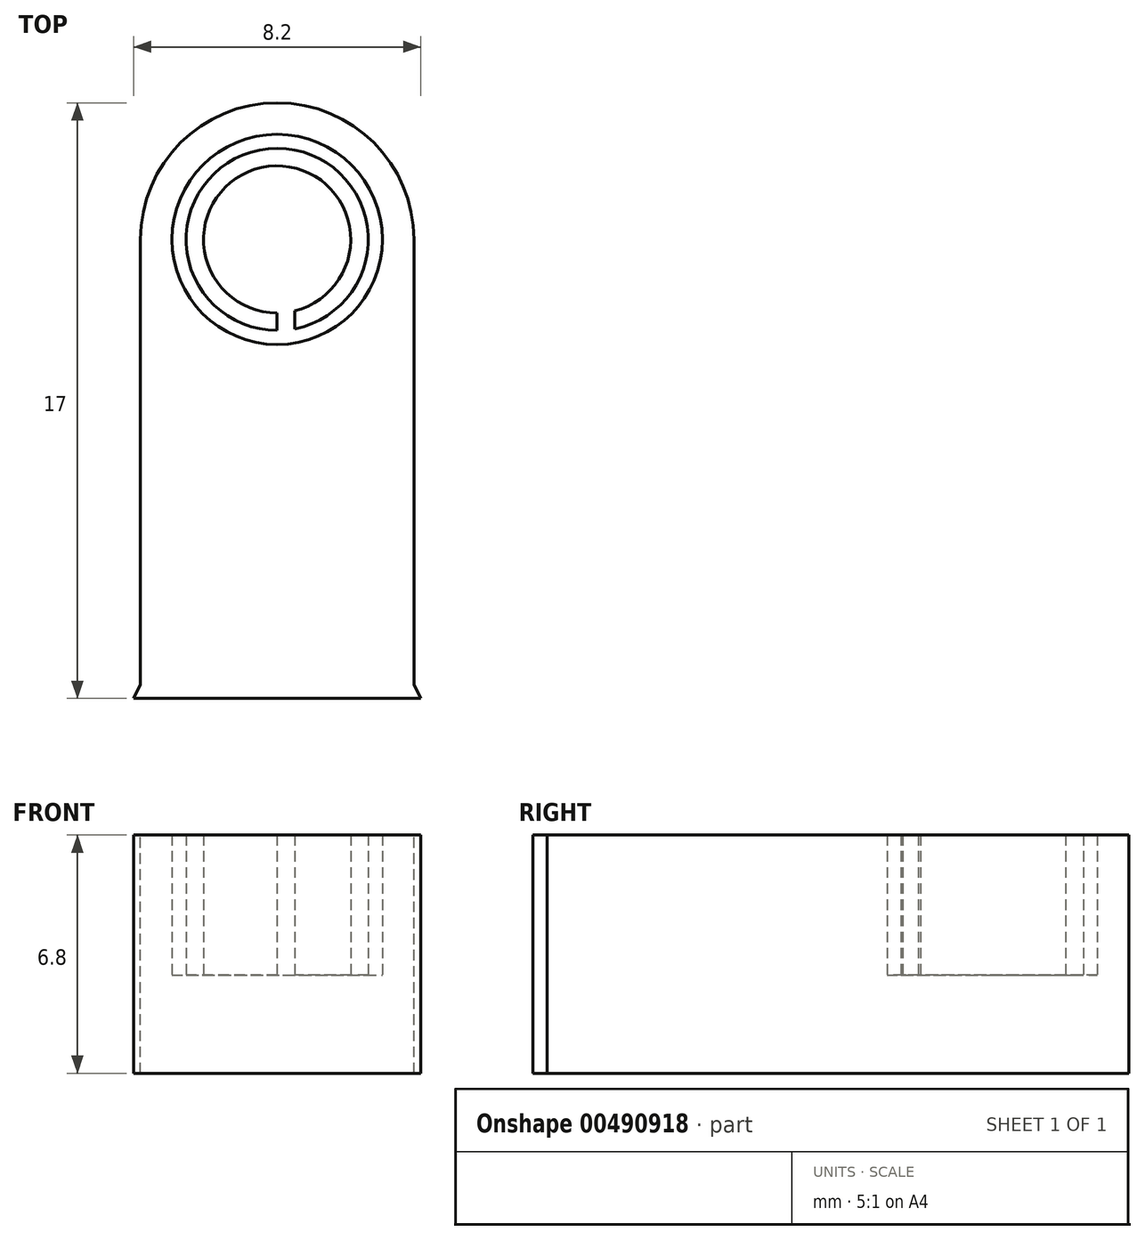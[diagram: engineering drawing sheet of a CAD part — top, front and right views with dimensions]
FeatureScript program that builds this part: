
annotation { "Feature Type Name" : "Feature", "Feature Type Description" : "" }
export const myFeature = defineFeature(function(context is Context, id is Id, definition is map)
    precondition{}
    {
        {
            var Q0;
            Q0=qCreatedBy(makeId("Top.planeOp"),FACE);
            var sketch = newSketch(context, id + "F0", { "sketchPlane" : qUnion([Q0])});
            skLineSegment(sketch, "E0", {"start": v(0, 0) * mm, "end": v(0, 12.7) * mm});
            skLineSegment(sketch, "E1", {"start": v(3.9, 16.6) * mm, "end": v(3.9, 16.6) * mm});
            skLineSegment(sketch, "E2", {"start": v(7.8, 12.7) * mm, "end": v(7.8, 0) * mm});
            skLineSegment(sketch, "E3", {"start": v(7.8, 0) * mm, "end": v(8, -0.4) * mm});
            skLineSegment(sketch, "E4", {"start": v(8, -0.4) * mm, "end": v(-0.2, -0.4) * mm});
            skLineSegment(sketch, "E5", {"start": v(-0.2, -0.4) * mm, "end": v(0, 0) * mm});
            skPoint(sketch, "E6.visualSharp", {"position": v(0, 16.6) * mm});
            skArc(sketch, "E6.filletArc", {"start": v(3.9, 16.6) * mm, "mid": v(1.14, 15.46) * mm, "end": v(0, 12.7) * mm});
            skPoint(sketch, "E7.visualSharp", {"position": v(7.8, 16.6) * mm});
            skArc(sketch, "E7.filletArc", {"start": v(7.8, 12.7) * mm, "mid": v(6.66, 15.46) * mm, "end": v(3.9, 16.6) * mm});
            skCircle(sketch, "E8", {"center": v(3.9, 12.7) * mm, "radius": 2.1 * mm});
            skCircle(sketch, "E9", {"center": v(3.9, 12.7) * mm, "radius": 2.6 * mm});
            skCircle(sketch, "E10", {"center": v(3.9, 12.7) * mm, "radius": 3 * mm});
            skLineSegment(sketch, "E11", {"start": v(3.9, 10.6) * mm, "end": v(3.9, 10.1) * mm});
            skLineSegment(sketch, "E12", {"start": v(3.4, 10.66) * mm, "end": v(3.4, 10.15) * mm});
            skSolve(sketch);
        }
        {
            var Q0;
            Q0=makeQuery(id+"F0.imprint","IMPRINT",FACE,{"disambiguationData":[TD([[makeQuery(id+"F0.imprint","IMPRINT",EDGE,{"derivedFrom":sQuery(id+"F0.wireOp",EDGE,"E0")}),-1.0]])]});
            var Q1;
            {var subQ0=sQuery(id+"F0.wireOp",EDGE,"E8");var subQ1=makeQuery(id+"F0.imprint","INTERSECT",VERTEX,{"derivedFrom":[subQ0,sQuery(id+"F0.wireOp",EDGE,"E11")]});Q1=makeQuery(id+"F0.imprint","IMPRINT",FACE,{"disambiguationData":[TD([[makeQuery(id+"F0.imprint","IMPRINT",EDGE,{"disambiguationData":[TD([[subQ1,1.0]])],"derivedFrom":subQ0}),1.0]])]});}
            var Q2;
            Q2=makeQuery(id+"F0.imprint","IMPRINT",FACE,{"disambiguationData":[TD([[makeQuery(id+"F0.imprint","IMPRINT",EDGE,{"derivedFrom":sQuery(id+"F0.wireOp",EDGE,"E10")}),1.0]])]});
            var Q3;
            {var subQ0=sQuery(id+"F0.wireOp",EDGE,"E11");Q3=makeQuery(id+"F0.imprint","IMPRINT",FACE,{"disambiguationData":[TD([[makeQuery(id+"F0.imprint","IMPRINT",EDGE,{"derivedFrom":subQ0}),1.0]])]});}
            var Q4;
            {var subQ0=sQuery(id+"F0.wireOp",EDGE,"E11");Q4=makeQuery(id+"F0.imprint","IMPRINT",FACE,{"disambiguationData":[TD([[makeQuery(id+"F0.imprint","IMPRINT",EDGE,{"derivedFrom":subQ0}),-1.0]])]});}
            extrude(context, id + "F1", {"entities" : qUnion([Q0, Q1, Q2, Q3, Q4]), "depth" : 2.8 * mm});
        }
        {
            var Q0;
            Q0 = qSketchRegion(id + "F0", true);
            var Q1;
            {var subQ0=sQuery(id+"F0.wireOp",EDGE,"E11");Q1=makeQuery(id+"F0.imprint","IMPRINT",FACE,{"disambiguationData":[TD([[makeQuery(id+"F0.imprint","IMPRINT",EDGE,{"derivedFrom":subQ0}),1.0]])]});}
            extrude(context, id + "F2", {"entities" : qUnion([Q0, Q1]), "operationType" : NewBodyOperationType.ADD, "oppositeDirection" : true, "depth" : 4 * mm});
        }
        {
            var Q0;
            Q0=makeQuery(id+"F1.opExtrude","SWEPT_BODY",BODY,{"disambiguationData":[OSD([sQuery(id+"F0.wireOp",EDGE,"E0"),sQuery(id+"F0.wireOp",EDGE,"E2"),sQuery(id+"F0.wireOp",EDGE,"AqsbTG2V-Ikan-dnIV-p5G3-8VfjzT4nuTyg"),sQuery(id+"F0.wireOp",EDGE,"E3"),sQuery(id+"F0.wireOp",EDGE,"E4"),sQuery(id+"F0.wireOp",EDGE,"E5"),sQuery(id+"F0.wireOp",EDGE,"v1Ig07qn-njf5-CgGw-4BEv-h1O8mq6ecXR5"),sQuery(id+"F0.wireOp",EDGE,"E6.filletArc"),sQuery(id+"F0.wireOp",EDGE,"E7.filletArc")])]});
            var Q1;
            Q1=makeQuery(id+"F1.opExtrude","CAP_EDGE",EDGE,{"disambiguationData":[OSD([sQuery(id+"F0.wireOp",EDGE,"E0")])],"isStart":false});
            transform(context, id + "F3", {"entities" : qUnion([Q0]), "transformType" : TransformType.ROTATION, "transformAxis" : qUnion([Q1]), "angle" : 180 * degree, "makeCopy" : false});
        }
    });
